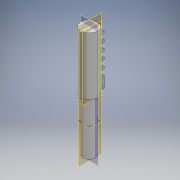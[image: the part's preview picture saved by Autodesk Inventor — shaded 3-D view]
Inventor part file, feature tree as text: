
AUTODESK INVENTOR PART (.ipt)
format: ipt  version: 2017 (Build 210142000, 142)  size: 299,520 bytes
history: native  units: mm
features: extrude x11, sketch x7, projected_geometry x5, other x2, pattern_linear x2
ambient origin geometry x8: Origin, YZ Plane, XZ Plane, XY Plane, X Axis, Y Axis, Z Axis, Center Point
bodies: Solide1 (feature_tree)
feature tree (27):
  extrude  "Extrusion1"  Depth=14.3mm
  extrude  "Extrusion2"  Depth=3.6mm
  sketch  "Esquisse4"
  other  "Plan de construction1"
  extrude  "Extrusion7"  Depth=7.2mm
  extrude  "Extrusion10"  Depth=40.0mm TaperAngle=0.0deg
  pattern_linear  "Réseau rectangulaire2"  Spacing1=0.8mm  [1 undecoded]
  extrude  "Extrusion11"  Depth=1.6mm
  pattern_linear  "Réseau rectangulaire3"  Spacing1=1.7mm  [1 undecoded]
  extrude  "Extrusion13"  Depth=10.0mm
  extrude  "Extrusion14"  Depth=10.0mm TaperAngle=0.0deg
  extrude  "Extrusion15"  Depth=4.25mm TaperAngle=0.0deg
  extrude  "Extrusion17"  Depth=6.8mm TaperAngle=0.0deg
  other  "Plan de construction2"
  extrude  "Extrusion18"  Depth=4.792891mm
  extrude  "Extrusion19"  Depth=70.0mm
  sketch  "Esquisse2"
  sketch  "Esquisse9"
  projected_geometry  "Boucle projetée8"
  sketch  "Esquisse13"
  projected_geometry  "Boucle projetée24"
  projected_geometry  "Boucle projetée25"
  projected_geometry  "Boucle projetée26"
  sketch  "Esquisse16"
  sketch  "Esquisse25"
  sketch  "Esquisse26"
  projected_geometry  "Boucle projetée28"
note: 2 required parameter values undecoded (feature->parameter linkage not recoverable at this tier; creation-order binding heuristic only, values carry confidence <= 0.55)
